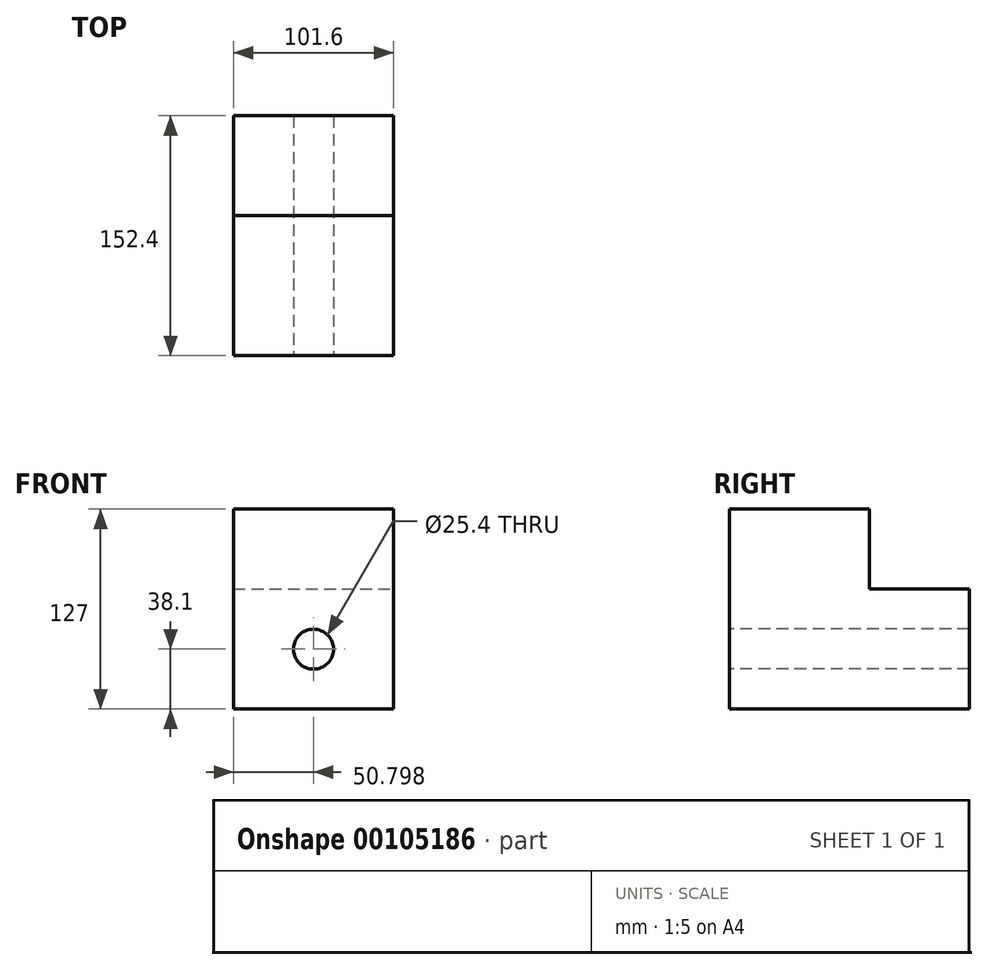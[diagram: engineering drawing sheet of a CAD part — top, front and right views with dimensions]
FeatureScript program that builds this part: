
annotation { "Feature Type Name" : "Feature", "Feature Type Description" : "" }
export const myFeature = defineFeature(function(context is Context, id is Id, definition is map)
    precondition{}
    {
        {
            var Q0;
            Q0=qCreatedBy(makeId("Top.planeOp"),FACE);
            var sketch = newSketch(context, id + "F0", { "sketchPlane" : qUnion([Q0])});
            skLineSegment(sketch, "E0.bottom", {"start": v(-66.94, 103.76) * mm, "end": v(34.66, 103.76) * mm});
            skLineSegment(sketch, "E0.top", {"start": v(-66.94, -48.64) * mm, "end": v(34.66, -48.64) * mm});
            skLineSegment(sketch, "E0.left", {"start": v(-66.94, 103.76) * mm, "end": v(-66.94, -48.64) * mm});
            skLineSegment(sketch, "E0.right", {"start": v(34.66, 103.76) * mm, "end": v(34.66, -48.64) * mm});
            skSolve(sketch);
        }
        {
            var Q0;
            Q0=makeQuery(id+"F0.imprint","IMPRINT",FACE,{"disambiguationData":[TD([[makeQuery(id+"F0.imprint","IMPRINT",EDGE,{"derivedFrom":sQuery(id+"F0.wireOp",EDGE,"E0.bottom")}),-1.0]])]});
            extrude(context, id + "F1", {"entities" : qUnion([Q0]), "depth" : 76.2 * mm});
        }
        {
            var Q0;
            Q0=makeQuery(id+"F1.opExtrude","CAP_FACE",FACE,{"disambiguationData":[OSD([sQuery(id+"F0.wireOp",EDGE,"E0.bottom"),sQuery(id+"F0.wireOp",EDGE,"E0.top"),sQuery(id+"F0.wireOp",EDGE,"E0.left"),sQuery(id+"F0.wireOp",EDGE,"E0.right")])],"isStart":false});
            var sketch = newSketch(context, id + "F2", { "sketchPlane" : qUnion([Q0])});
            skLineSegment(sketch, "E1.bottom", {"start": v(-66.94, -48.64) * mm, "end": v(34.66, -48.64) * mm});
            skLineSegment(sketch, "E1.top", {"start": v(-66.94, 40.26) * mm, "end": v(34.66, 40.26) * mm});
            skLineSegment(sketch, "E1.left", {"start": v(-66.94, -48.64) * mm, "end": v(-66.94, 40.26) * mm});
            skLineSegment(sketch, "E1.right", {"start": v(34.66, -48.64) * mm, "end": v(34.66, 40.26) * mm});
            skSolve(sketch);
        }
        {
            var Q0;
            Q0=makeQuery(id+"F2.imprint","IMPRINT",FACE,{"disambiguationData":[TD([[makeQuery(id+"F2.imprint","IMPRINT",EDGE,{"derivedFrom":sQuery(id+"F2.wireOp",EDGE,"E1.bottom")}),1.0]])]});
            extrude(context, id + "F3", {"entities" : qUnion([Q0]), "operationType" : NewBodyOperationType.ADD, "depth" : 50.8 * mm});
        }
        {
            var Q0;
            Q0=makeQuery(id+"F3.boolean.opBoolean","MERGE",FACE,{"derivedFrom":[makeQuery(id+"F1.opExtrude","SWEPT_FACE",FACE,{"disambiguationData":[OSD([sQuery(id+"F0.wireOp",EDGE,"E0.top")])]}),makeQuery(id+"F3.opExtrude","SWEPT_FACE",FACE,{"disambiguationData":[OSD([sQuery(id+"F2.wireOp",EDGE,"E1.bottom")])]})]});
            var sketch = newSketch(context, id + "F4", { "sketchPlane" : qUnion([Q0])});
            skLineSegment(sketch, "E2.bottom", {"start": v(-66.94, 0) * mm, "end": v(-16.14, 0) * mm});
            skLineSegment(sketch, "E2.top", {"start": v(-66.94, 38.1) * mm, "end": v(-16.14, 38.1) * mm});
            skLineSegment(sketch, "E2.left", {"start": v(-66.94, 0) * mm, "end": v(-66.94, 38.1) * mm});
            skLineSegment(sketch, "E2.right", {"start": v(-16.14, 0) * mm, "end": v(-16.14, 38.1) * mm});
            skSolve(sketch);
        }
        {
            var Q0;
            Q0=sQuery(id+"F4.wireOp",VERTEX,"E2.top.end");
            var Q1;
            Q1=makeQuery(id+"F1.opExtrude","SWEPT_BODY",BODY,{"disambiguationData":[OSD([sQuery(id+"F0.wireOp",EDGE,"E0.bottom"),sQuery(id+"F0.wireOp",EDGE,"E0.top"),sQuery(id+"F0.wireOp",EDGE,"E0.left"),sQuery(id+"F0.wireOp",EDGE,"E0.right")])]});
            hole(context, id + "F5", {"style" : HoleStyle.SIMPLE, "endStyle" : HoleEndStyle.THROUGH, "holeDiameter" : 25.4 * mm, "locations" : qUnion([Q0]), "scope" : qUnion([Q1]), "isTappedThrough" : true});
        }
    });
